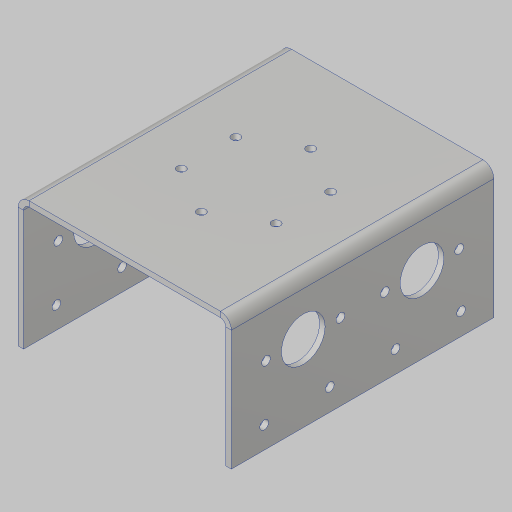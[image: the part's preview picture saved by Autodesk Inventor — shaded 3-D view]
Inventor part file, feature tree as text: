
AUTODESK INVENTOR PART (.ipt)
format: ipt  version: 2023.5 (Build 275446000, 446)  size: 198,144 bytes
history: native  units: in
note: dims shown in document units (in); Inventor stores cm internally (conversion verified against a paired STEP export)
features: sketch x6, sheet_metal_op x4, hole x4, other x2, pattern_circular x1, projected_geometry x1
ambient origin geometry x8: Origin, YZ Plane, XZ Plane, XY Plane, X Axis, Y Axis, Z Axis, Center Point
bodies: Solid1 (feature_tree)
feature tree (18):
  sheet_metal_op  "Face1"
  sheet_metal_op  "Flange1"
  hole  "Hole1"  [1 undecoded]
  hole  "Hole2"  [1 undecoded]
  pattern_circular  "Circular Pattern1"  [2 undecoded]
  hole  "Hole3"  [1 undecoded]
  hole  "Hole4"  [1 undecoded]
  sketch  "Sketch1"  dims[d0=6.0in d1=4.875in]
  other  "Plate1"
  sketch  "Sketch3"  dims[d2=0.125in d4=0.125in]
  other  "Plate2"
  sheet_metal_op  "Bend1"
  sheet_metal_op  "Corner1"
  sketch  "Sketch4"  dims[d5=0.0625in]
  sketch  "Sketch5"  dims[d6=0.25in]
  sketch  "Sketch6"  dims[d7=0.125in]
  sketch  "Sketch7"  dims[d8=3.0in d9=90.0deg d10=0.125in d11=0.5in d12=0.125in d13=0.125in d14=1.25in d15=2.716in d17=1.0in d18=0.38in d19=0.375in d20=0.25in d21=0.5635in d22=0.125in d23=0.0in d24=2.5in d25=0.201in d26=0.75in d27=0.385in d28=0.25in d29=0.5635in d30=0.125in d31=0.8108in d32=2.3622in d33=360.0deg d35=1.5in d36=1.5in d37=1.5in d38=0.5in d39=0.201in d40=0.75in d41=0.385in d42=0.25in d43=0.5635in d44=0.125in d45=0.8108in d46=1.7in d47=1.7in d48=0.201in d49=0.38in d50=0.385in d51=0.25in d52=0.5635in d53=0.125in d54=0.8108in]
  projected_geometry  "Project Cut Edges2"
note: 6 required parameter values undecoded (feature->parameter linkage not recoverable at this tier; creation-order binding heuristic only, values carry confidence <= 0.55)
